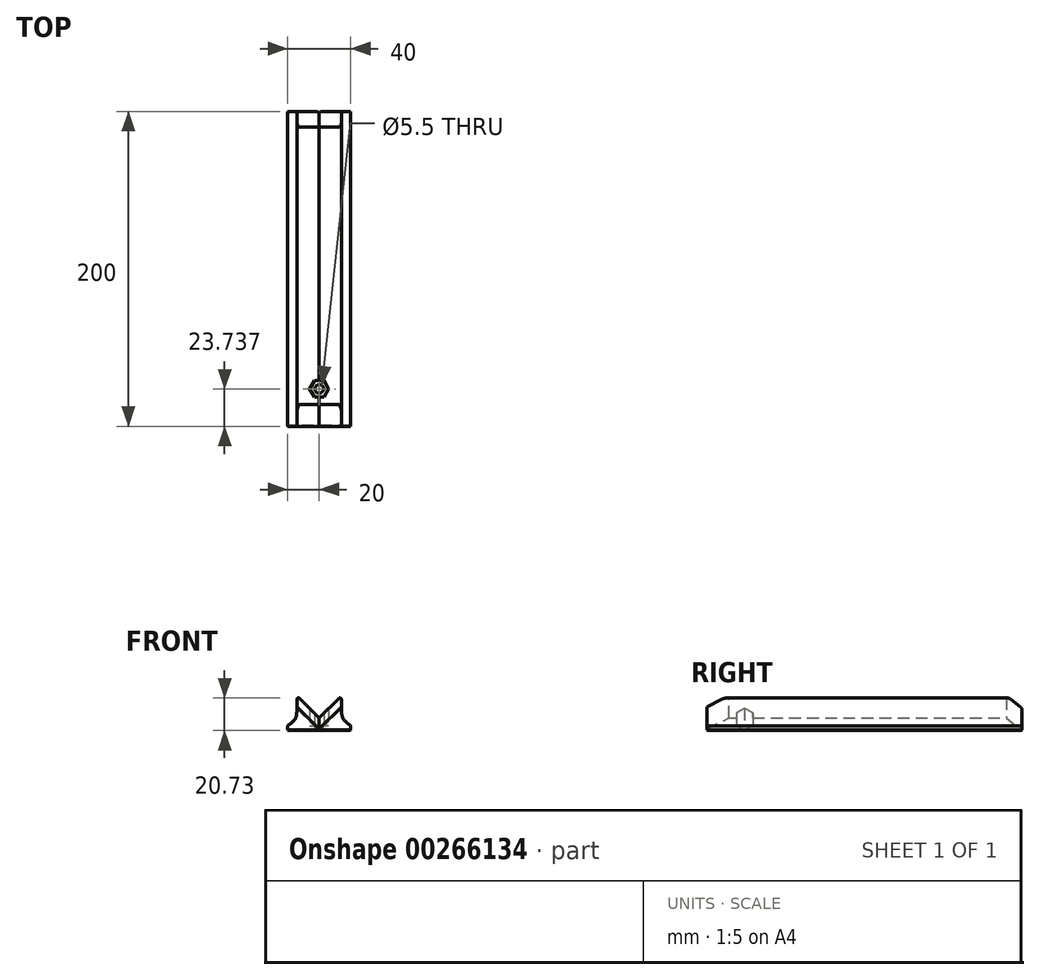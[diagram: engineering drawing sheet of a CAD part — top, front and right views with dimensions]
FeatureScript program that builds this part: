
annotation { "Feature Type Name" : "Feature", "Feature Type Description" : "" }
export const myFeature = defineFeature(function(context is Context, id is Id, definition is map)
    precondition{}
    {
        {
            var Q0;
            Q0=qCreatedBy(makeId("Front.planeOp"),FACE);
            var sketch = newSketch(context, id + "F0", { "sketchPlane" : qUnion([Q0])});
            skLineSegment(sketch, "E0", {"start": v(-20, 0) * mm, "end": v(20, 0) * mm});
            skLineSegment(sketch, "E1", {"start": v(20, 0) * mm, "end": v(20, 3) * mm});
            skLineSegment(sketch, "E2", {"start": v(20, 3) * mm, "end": v(14.14, 3) * mm});
            skLineSegment(sketch, "E3", {"start": v(14.14, 3) * mm, "end": v(14.14, 22.14) * mm});
            skLineSegment(sketch, "E4", {"start": v(14.14, 22.14) * mm, "end": v(0, 8) * mm});
            skLineSegment(sketch, "E5", {"start": v(0, 8) * mm, "end": v(-14.14, 22.14) * mm});
            skLineSegment(sketch, "E6", {"start": v(-14.14, 22.14) * mm, "end": v(-14.14, 3) * mm});
            skLineSegment(sketch, "E7", {"start": v(-14.14, 3) * mm, "end": v(-20, 3) * mm});
            skLineSegment(sketch, "E8", {"start": v(-20, 3) * mm, "end": v(-20, 0) * mm});
            skSolve(sketch);
        }
        {
            var Q0;
            Q0=makeQuery(id+"F0.imprint","IMPRINT",FACE,{"disambiguationData":[TD([[makeQuery(id+"F0.imprint","IMPRINT",EDGE,{"derivedFrom":sQuery(id+"F0.wireOp",EDGE,"E0")}),1.0]])]});
            extrude(context, id + "F1", {"entities" : qUnion([Q0]), "depth" : 200 * mm});
        }
        {
            var Q0;
            Q0=makeQuery(id+"F1.opExtrude","SWEPT_EDGE",EDGE,{"disambiguationData":[OSD([sQuery(id+"F0.wireOp",EDGE,"E6"),sQuery(id+"F0.wireOp",EDGE,"E7")])]});
            var Q1;
            Q1=makeQuery(id+"F1.opExtrude","SWEPT_EDGE",EDGE,{"disambiguationData":[OSD([sQuery(id+"F0.wireOp",EDGE,"E2"),sQuery(id+"F0.wireOp",EDGE,"E3")])]});
            fillet(context, id + "F2", {"entities" : qUnion([Q0, Q1]), "radius" : 15 * mm, "tangentPropagation" : true, "rho" : 0.7, "crossSection" : FilletCrossSection.CONIC, "allowEdgeOverflow" : false});
        }
        {
            var Q0;
            Q0=makeQuery(id+"F1.opExtrude","CAP_EDGE",EDGE,{"disambiguationData":[OSD([sQuery(id+"F0.wireOp",EDGE,"E5")])],"isStart":false});
            var Q1;
            Q1=makeQuery(id+"F1.opExtrude","CAP_EDGE",EDGE,{"disambiguationData":[OSD([sQuery(id+"F0.wireOp",EDGE,"E4")])],"isStart":false});
            chamfer(context, id + "F3", {"entities" : qUnion([Q0, Q1]), "chamferType" : ChamferType.OFFSET_ANGLE, "width" : 5 * mm, "oppositeDirection" : false, "angle" : 70 * degree, "tangentPropagation" : true});
        }
        {
            var Q0;
            Q0=makeQuery(id+"F1.opExtrude","CAP_EDGE",EDGE,{"disambiguationData":[OSD([sQuery(id+"F0.wireOp",EDGE,"E4")])],"isStart":true});
            var Q1;
            Q1=makeQuery(id+"F1.opExtrude","CAP_EDGE",EDGE,{"disambiguationData":[OSD([sQuery(id+"F0.wireOp",EDGE,"E5")])],"isStart":true});
            chamfer(context, id + "F4", {"entities" : qUnion([Q0, Q1]), "chamferType" : ChamferType.OFFSET_ANGLE, "width" : 10 * mm, "oppositeDirection" : false, "angle" : 30 * degree, "tangentPropagation" : true});
        }
        {
            var Q0;
            Q0=makeQuery(id+"F1.opExtrude","SWEPT_FACE",FACE,{"disambiguationData":[OSD([sQuery(id+"F0.wireOp",EDGE,"E0")])]});
            chamfer(context, id + "F5", {"entities" : qUnion([Q0]), "width" : .5 * mm, "tangentPropagation" : true});
        }
        {
            var Q0;
            Q0=makeQuery(id+"F1.opExtrude","SWEPT_EDGE",EDGE,{"disambiguationData":[OSD([sQuery(id+"F0.wireOp",EDGE,"E5"),sQuery(id+"F0.wireOp",EDGE,"E6")])]});
            var Q1;
            Q1=makeQuery(id+"F1.opExtrude","SWEPT_EDGE",EDGE,{"disambiguationData":[OSD([sQuery(id+"F0.wireOp",EDGE,"E3"),sQuery(id+"F0.wireOp",EDGE,"E4")])]});
            fillet(context, id + "F6", {"entities" : qUnion([Q0, Q1]), "radius" : 1 * mm, "tangentPropagation" : true, "allowEdgeOverflow" : false});
        }
        {
            var Q0;
            Q0=qCreatedBy(makeId("Top.planeOp"),FACE);
            cPlane(context, id + "F7", {"entities" : qUnion([Q0]), "cplaneType" : CPlaneType.OFFSET, "offset" : 8 * mm, "width" : 150 * mm, "height" : 150 * mm});
        }
        {
            var Q0;
            Q0=qCreatedBy(id+"F7.planeOp",FACE);
            var sketch = newSketch(context, id + "F8", { "sketchPlane" : qUnion([Q0])});
            skPoint(sketch, "E9", {"position": v(0, -176.26) * mm});
            skSolve(sketch);
        }
        {
            var Q0;
            Q0=qCreatedBy(id+"F7.planeOp",FACE);
            var sketch = newSketch(context, id + "F9", { "sketchPlane" : qUnion([Q0])});
            skCircle(sketch, "E10.cCircle", {"center": v(0, -176.26) * mm, "radius": 5.25 * mm, "construction": true});
            skLineSegment(sketch, "E10.0", {"start": v(6.06, -176.26) * mm, "end": v(3.03, -181.51) * mm});
            skLineSegment(sketch, "E10.1", {"start": v(3.03, -181.51) * mm, "end": v(-3.03, -181.51) * mm});
            skLineSegment(sketch, "E10.2", {"start": v(-3.03, -181.51) * mm, "end": v(-6.06, -176.26) * mm});
            skLineSegment(sketch, "E10.3", {"start": v(-6.06, -176.26) * mm, "end": v(-3.03, -171.01) * mm});
            skLineSegment(sketch, "E10.4", {"start": v(-3.03, -171.01) * mm, "end": v(3.03, -171.01) * mm});
            skLineSegment(sketch, "E10.5", {"start": v(3.03, -171.01) * mm, "end": v(6.06, -176.26) * mm});
            skPoint(sketch, "E10.0.midPoint", {"position": v(4.55, -178.89) * mm});
            skSolve(sketch);
        }
        {
            var Q0;
            Q0=makeQuery(id+"F9.imprint","IMPRINT",FACE,{"disambiguationData":[TD([[makeQuery(id+"F9.imprint","IMPRINT",EDGE,{"derivedFrom":sQuery(id+"F9.wireOp",EDGE,"E10.0")}),-1.0]])]});
            extrude(context, id + "F10", {"entities" : qUnion([Q0]), "operationType" : NewBodyOperationType.REMOVE, "depth" : 25 * mm, "hasSecondDirection" : true, "secondDirectionOppositeDirection" : true, "secondDirectionDepth" : 5 * mm});
        }
        {
            var Q0;
            Q0=makeQuery(id+"F10.boolean.opBoolean","COPY",FACE,{"derivedFrom":makeQuery(id+"F10.opExtrude","CAP_FACE",FACE,{"disambiguationData":[OSD([sQuery(id+"F9.wireOp",EDGE,"E10.0"),sQuery(id+"F9.wireOp",EDGE,"E10.1"),sQuery(id+"F9.wireOp",EDGE,"E10.2"),sQuery(id+"F9.wireOp",EDGE,"E10.3"),sQuery(id+"F9.wireOp",EDGE,"E10.4"),sQuery(id+"F9.wireOp",EDGE,"E10.5")])],"isStart":true})});
            var sketch = newSketch(context, id + "F11", { "sketchPlane" : qUnion([Q0])});
            skCircle(sketch, "E11", {"center": v(0, -176.26) * mm, "radius": 2.75 * mm});
            skSolve(sketch);
        }
        {
            var Q0;
            Q0=makeQuery(id+"F11.imprint","IMPRINT",FACE,{"disambiguationData":[TD([[makeQuery(id+"F11.imprint","IMPRINT",EDGE,{"derivedFrom":sQuery(id+"F11.wireOp",EDGE,"E11")}),1.0]])]});
            extrude(context, id + "F12", {"entities" : qUnion([Q0]), "operationType" : NewBodyOperationType.REMOVE, "oppositeDirection" : true, "depth" : 25 * mm});
        }
    });
